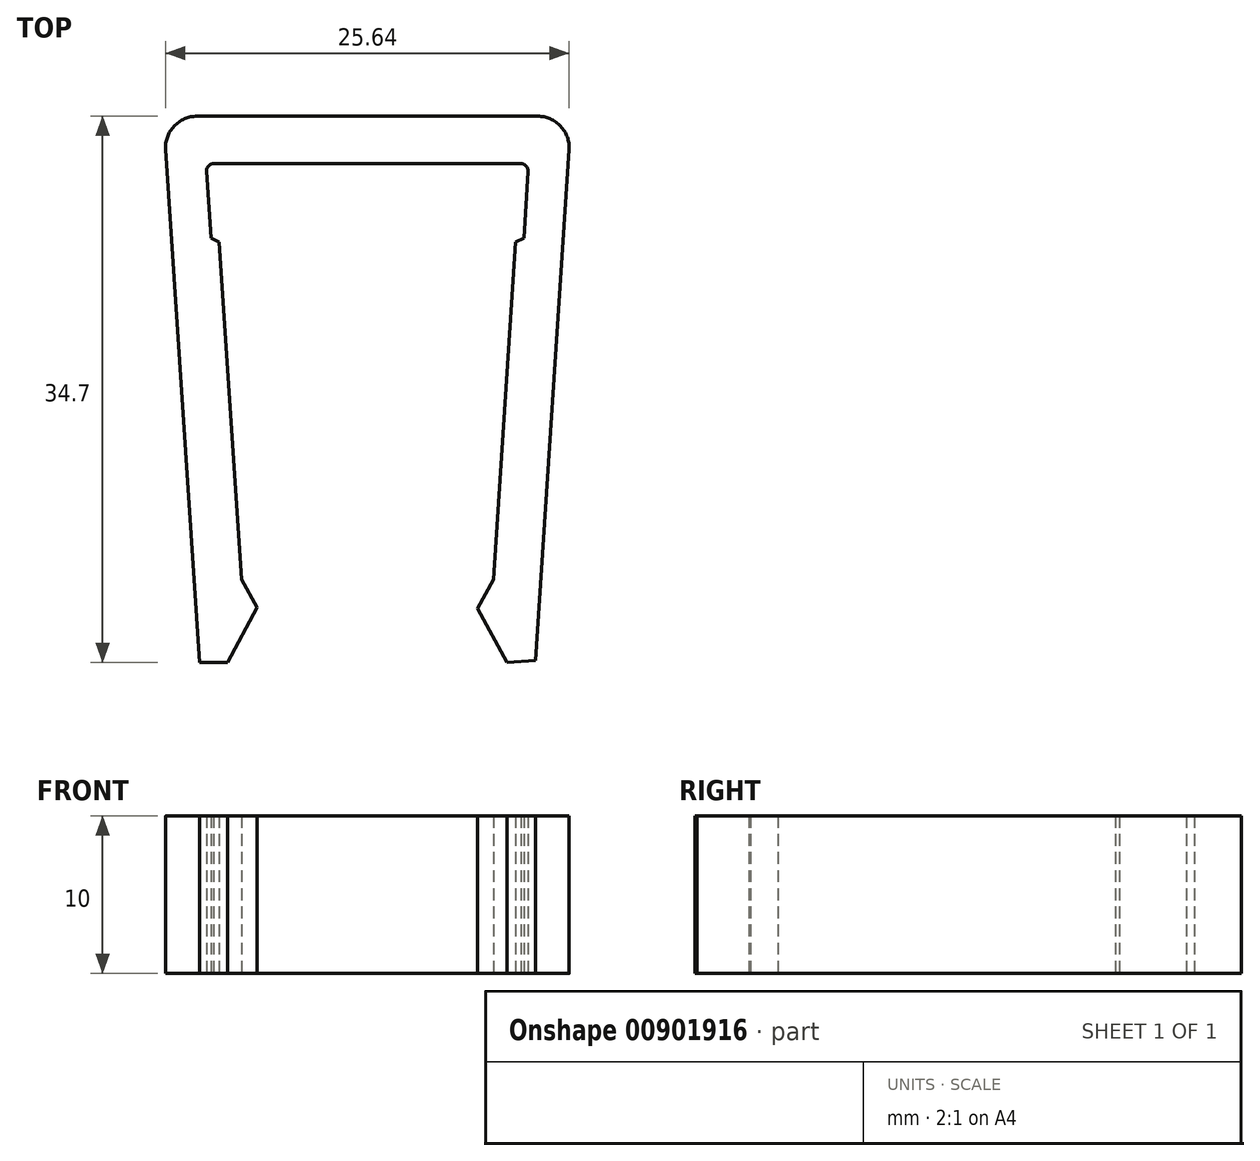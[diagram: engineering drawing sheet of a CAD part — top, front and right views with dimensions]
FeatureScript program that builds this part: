
annotation { "Feature Type Name" : "Feature", "Feature Type Description" : "" }
export const myFeature = defineFeature(function(context is Context, id is Id, definition is map)
    precondition{}
    {
        {
            var Q0;
            Q0=qCreatedBy(makeId("Top.planeOp"),FACE);
            var sketch = newSketch(context, id + "F0", { "sketchPlane" : qUnion([Q0])});
            skLineSegment(sketch, "E0", {"start": v(-9.75, 18.57) * mm, "end": v(9.75, 18.57) * mm});
            skLineSegment(sketch, "E1", {"start": v(9.75, 18.57) * mm, "end": v(9.75, 18.57) * mm});
            skLineSegment(sketch, "E2", {"start": v(-8, -7.88) * mm, "end": v(-9.42, 13.57) * mm});
            skLineSegment(sketch, "E3", {"start": v(-10.66, -13.13) * mm, "end": v(-12.81, 19.43) * mm});
            skLineSegment(sketch, "E4", {"start": v(-10.82, 21.57) * mm, "end": v(10.82, 21.57) * mm});
            skLineSegment(sketch, "E5", {"start": v(12.81, 19.43) * mm, "end": v(10.67, -13.02) * mm});
            skLineSegment(sketch, "E6", {"start": v(-8, -7.88) * mm, "end": v(-8, -9.63) * mm, "construction": true});
            skLineSegment(sketch, "E7", {"start": v(-8, -9.63) * mm, "end": v(-7, -9.63) * mm, "construction": true});
            skLineSegment(sketch, "E8", {"start": v(-8, -7.88) * mm, "end": v(-7, -9.63) * mm});
            skLineSegment(sketch, "E9", {"start": v(-7, -9.63) * mm, "end": v(-8.87, -13.13) * mm});
            skLineSegment(sketch, "E10", {"start": v(-8.87, -13.13) * mm, "end": v(-10.66, -13.13) * mm});
            skPoint(sketch, "E11.orphan", {"position": v(-10.37, -17.55) * mm});
            skLineSegment(sketch, "E12", {"start": v(8, -7.88) * mm, "end": v(8, -9.7) * mm, "construction": true});
            skLineSegment(sketch, "E13", {"start": v(8, -9.7) * mm, "end": v(7, -9.7) * mm, "construction": true});
            skLineSegment(sketch, "E14", {"start": v(8, -7.88) * mm, "end": v(7, -9.7) * mm});
            skLineSegment(sketch, "E15", {"start": v(7, -9.7) * mm, "end": v(8.88, -13.13) * mm});
            skLineSegment(sketch, "E16", {"start": v(8.88, -13.13) * mm, "end": v(10.67, -13.02) * mm});
            skPoint(sketch, "E17.orphan", {"position": v(10.37, -17.55) * mm});
            skPoint(sketch, "E18", {"position": v(9.42, 13.57) * mm});
            skPoint(sketch, "E19", {"position": v(-9.42, 13.57) * mm});
            skLineSegment(sketch, "E20", {"start": v(-10.22, 18.07) * mm, "end": v(-9.94, 13.82) * mm});
            skLineSegment(sketch, "E21", {"start": v(10.22, 18.03) * mm, "end": v(9.94, 13.82) * mm});
            skPoint(sketch, "E22", {"position": v(-9.72, 18.07) * mm});
            skArc(sketch, "E23", {"start": v(-9.75, 18.57) * mm, "mid": v(-10.08, 18.4) * mm, "end": v(-10.22, 18.07) * mm});
            skPoint(sketch, "E24", {"position": v(9.72, 18.07) * mm});
            skArc(sketch, "E25", {"start": v(10.22, 18.03) * mm, "mid": v(10.1, 18.4) * mm, "end": v(9.75, 18.57) * mm});
            skLineSegment(sketch, "E26", {"start": v(9.42, 13.57) * mm, "end": v(9.94, 13.82) * mm});
            skLineSegment(sketch, "E27", {"start": v(-9.42, 13.57) * mm, "end": v(-9.94, 13.82) * mm});
            skLineSegment(sketch, "E28.trimOffspring", {"start": v(9.42, 13.57) * mm, "end": v(8, -7.88) * mm});
            skPoint(sketch, "E29.visualSharp", {"position": v(-12.96, 21.57) * mm});
            skArc(sketch, "E29.filletArc", {"start": v(-10.82, 21.57) * mm, "mid": v(-12.28, 20.93) * mm, "end": v(-12.81, 19.43) * mm});
            skPoint(sketch, "E30.visualSharp", {"position": v(12.96, 21.57) * mm});
            skArc(sketch, "E30.filletArc", {"start": v(12.81, 19.43) * mm, "mid": v(12.28, 20.93) * mm, "end": v(10.82, 21.57) * mm});
            skSolve(sketch);
        }
        {
            var Q0;
            Q0=makeQuery(id+"F0.imprint","IMPRINT",FACE,{"disambiguationData":[TD([[makeQuery(id+"F0.imprint","IMPRINT",EDGE,{"derivedFrom":sQuery(id+"F0.wireOp",EDGE,"E0")}),1.0]])]});
            extrude(context, id + "F1", {"entities" : qUnion([Q0]), "depth" : 10 * mm, "offsetDistance" : 25 * mm});
        }
    });
